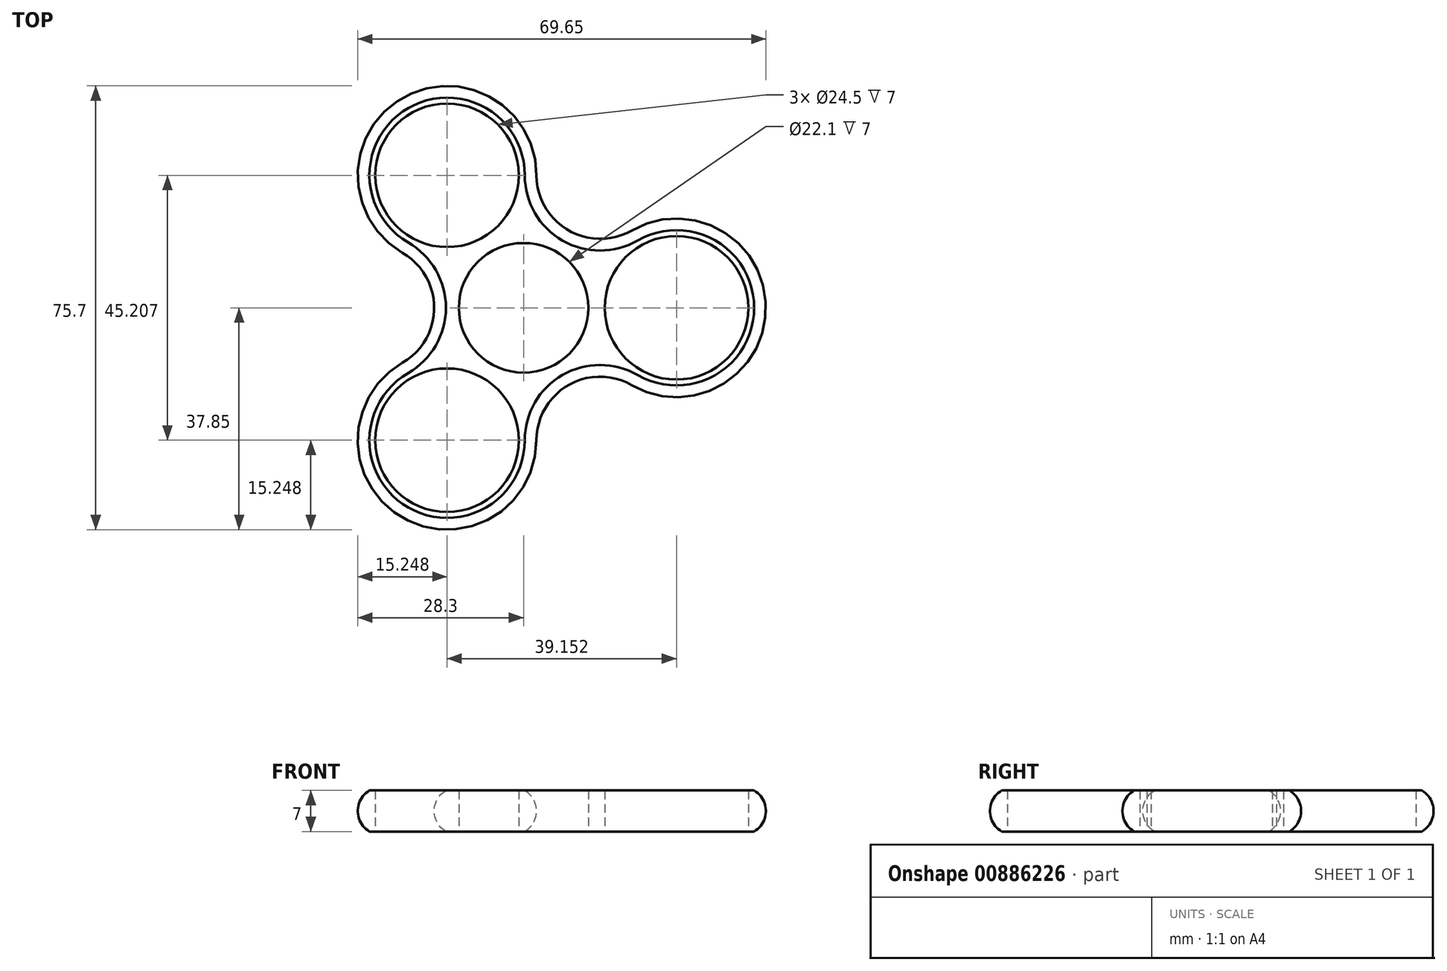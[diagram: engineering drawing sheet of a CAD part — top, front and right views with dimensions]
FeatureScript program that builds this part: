
annotation { "Feature Type Name" : "Feature", "Feature Type Description" : "" }
export const myFeature = defineFeature(function(context is Context, id is Id, definition is map)
    precondition{}
    {
        {
            var Q0;
            Q0=qCreatedBy(makeId("Top.planeOp"),FACE);
            var sketch = newSketch(context, id + "F0", { "sketchPlane" : qUnion([Q0])});
            skCircle(sketch, "E0", {"center": v(0, 0) * mm, "radius": 11.05 * mm});
            skCircle(sketch, "E1", {"center": v(26.1, 0) * mm, "radius": 12.25 * mm});
            skCircle(sketch, "E2", {"center": v(0, 0) * mm, "radius": 26.1 * mm, "construction": true});
            skCircle(sketch, "E3.0", {"center": v(26.1, 0) * mm, "radius": 13.25 * mm});
            skCircle(sketch, "E4.1.0", {"center": v(-13.05, 22.6) * mm, "radius": 13.25 * mm});
            skCircle(sketch, "E4.1.1", {"center": v(-13.05, 22.6) * mm, "radius": 12.25 * mm});
            skCircle(sketch, "E4.2.0", {"center": v(-13.05, -22.6) * mm, "radius": 13.25 * mm});
            skCircle(sketch, "E4.2.1", {"center": v(-13.05, -22.6) * mm, "radius": 12.25 * mm});
            skLineSegment(sketch, "E5", {"start": v(-13.05, 22.6) * mm, "end": v(13.05, -22.6) * mm, "construction": true});
            skLineSegment(sketch, "E6", {"start": v(-13.05, -22.6) * mm, "end": v(13.05, -22.6) * mm, "construction": true});
            skLineSegment(sketch, "E7", {"start": v(13.05, -22.6) * mm, "end": v(26.1, 0) * mm, "construction": true});
            skArc(sketch, "E8", {"start": v(19.47, -11.48) * mm, "mid": v(6.62, -11.48) * mm, "end": v(0.2, -22.6) * mm});
            skArc(sketch, "E9.1.0", {"start": v(0.2, 22.6) * mm, "mid": v(6.63, 11.47) * mm, "end": v(19.48, 11.47) * mm});
            skArc(sketch, "E9.2.0", {"start": v(-19.68, -11.13) * mm, "mid": v(-13.25, 0) * mm, "end": v(-19.67, 11.13) * mm});
            skLineSegment(sketch, "E10", {"start": v(0, 0) * mm, "end": v(26.1, 0) * mm, "construction": true});
            skLineSegment(sketch, "E11", {"start": v(-13.05, 22.6) * mm, "end": v(0, 0) * mm, "construction": true});
            skLineSegment(sketch, "E12", {"start": v(0, 0) * mm, "end": v(-13.05, -22.6) * mm, "construction": true});
            skSolve(sketch);
        }
        {
            var Q0;
            Q0=makeQuery(id+"F0.imprint","IMPRINT",FACE,{"disambiguationData":[TD([[makeQuery(id+"F0.imprint","IMPRINT",EDGE,{"derivedFrom":sQuery(id+"F0.wireOp",EDGE,"E0")}),-1.0]])]});
            var Q1;
            Q1=makeQuery(id+"F0.imprint","IMPRINT",FACE,{"disambiguationData":[TD([[makeQuery(id+"F0.imprint","IMPRINT",EDGE,{"derivedFrom":sQuery(id+"F0.wireOp",EDGE,"E4.1.1")}),-1.0]])]});
            var Q2;
            Q2=makeQuery(id+"F0.imprint","IMPRINT",FACE,{"disambiguationData":[TD([[makeQuery(id+"F0.imprint","IMPRINT",EDGE,{"derivedFrom":sQuery(id+"F0.wireOp",EDGE,"E1")}),-1.0]])]});
            var Q3;
            Q3=makeQuery(id+"F0.imprint","IMPRINT",FACE,{"disambiguationData":[TD([[makeQuery(id+"F0.imprint","IMPRINT",EDGE,{"derivedFrom":sQuery(id+"F0.wireOp",EDGE,"E4.2.1")}),-1.0]])]});
            extrude(context, id + "F1", {"entities" : qUnion([Q0, Q1, Q2, Q3]), "depth" : 7 * mm, "offsetDistance" : 25 * mm});
        }
        {
            var Q0;
            Q0=qCreatedBy(makeId("Front.planeOp"),FACE);
            var sketch = newSketch(context, id + "F2", { "sketchPlane" : qUnion([Q0])});
            skPoint(sketch, "E13.0", {"position": v(39.35, 7) * mm});
            skPoint(sketch, "E14.0", {"position": v(39.35, 0) * mm});
            skArc(sketch, "E15", {"start": v(39.35, 0) * mm, "mid": v(41.35, 3.5) * mm, "end": v(39.35, 7) * mm});
            skLineSegment(sketch, "E16", {"start": v(39.35, 7) * mm, "end": v(39.35, 0) * mm});
            skPoint(sketch, "E17", {"position": v(39.35, 3.5) * mm});
            skPoint(sketch, "E18", {"position": v(41.35, 3.5) * mm});
            skSolve(sketch);
        }
        {
            var Q0;
            Q0=makeQuery(id+"F2.imprint","IMPRINT",FACE,{"disambiguationData":[TD([[makeQuery(id+"F2.imprint","IMPRINT",EDGE,{"derivedFrom":sQuery(id+"F2.wireOp",EDGE,"s32fWGcO-ubQ4-Y1d4-2bjF-cBnH2Gjxc5p4")}),1.0]])]});
            var Q1;
            Q1=makeQuery(id+"F2.imprint","IMPRINT",FACE,{"disambiguationData":[TD([[makeQuery(id+"F2.imprint","IMPRINT",EDGE,{"derivedFrom":sQuery(id+"F2.wireOp",EDGE,"E15")}),1.0]])]});
            var Q2;
            Q2=makeQuery(id+"F1.opExtrude","CAP_EDGE",EDGE,{"disambiguationData":[OSD([sQuery(id+"F0.wireOp",EDGE,"E3.0")])],"isStart":false});
            var Q3;
            Q3=makeQuery(id+"F1.opExtrude","CAP_EDGE",EDGE,{"disambiguationData":[OSD([sQuery(id+"F0.wireOp",EDGE,"E8")])],"isStart":false});
            var Q4;
            Q4=makeQuery(id+"F1.opExtrude","CAP_EDGE",EDGE,{"disambiguationData":[OSD([sQuery(id+"F0.wireOp",EDGE,"E4.2.0")])],"isStart":false});
            var Q5;
            Q5=makeQuery(id+"F1.opExtrude","CAP_EDGE",EDGE,{"disambiguationData":[OSD([sQuery(id+"F0.wireOp",EDGE,"E4.1.0")])],"isStart":false});
            var Q6;
            Q6=makeQuery(id+"F1.opExtrude","CAP_EDGE",EDGE,{"disambiguationData":[OSD([sQuery(id+"F0.wireOp",EDGE,"E9.2.0")])],"isStart":false});
            var Q7;
            Q7=makeQuery(id+"F1.opExtrude","CAP_EDGE",EDGE,{"disambiguationData":[OSD([sQuery(id+"F0.wireOp",EDGE,"E9.1.0")])],"isStart":false});
            sweep(context, id + "F3", {"operationType" : NewBodyOperationType.ADD, "profiles" : qUnion([Q0, Q1]), "path" : qUnion([Q2, Q3, Q4, Q5, Q6, Q7])});
        }
    });
